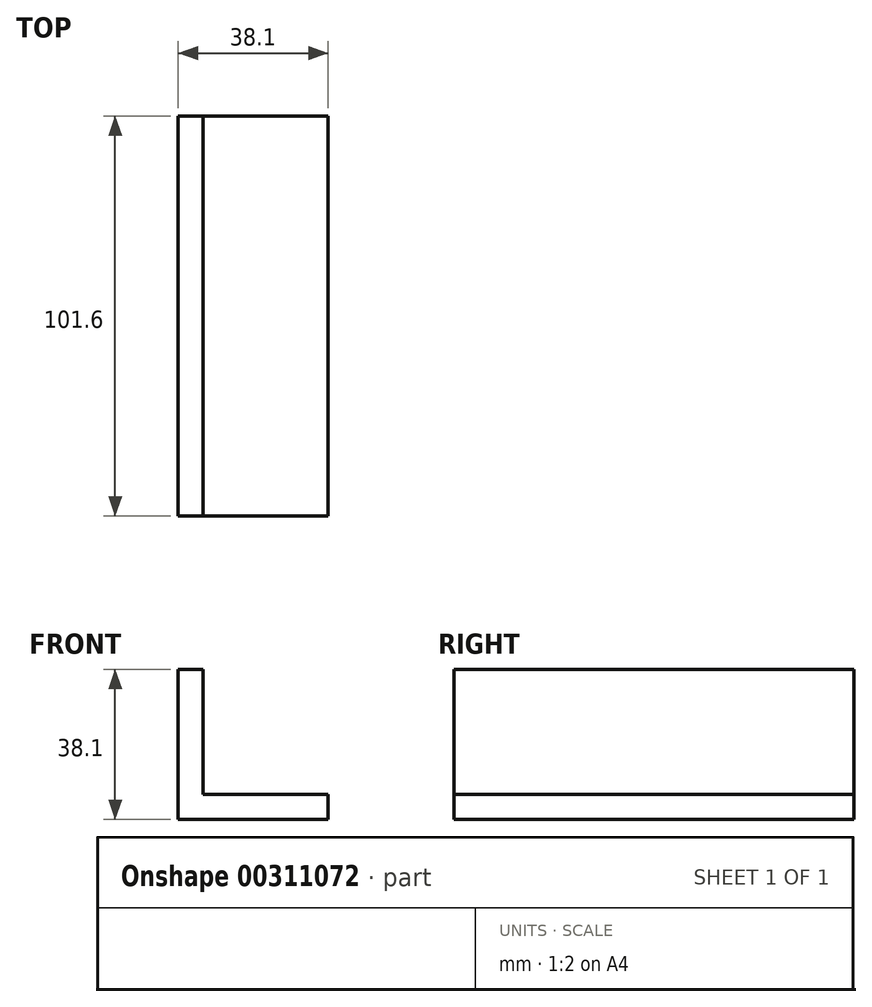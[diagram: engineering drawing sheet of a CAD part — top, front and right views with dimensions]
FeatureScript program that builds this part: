
annotation { "Feature Type Name" : "Feature", "Feature Type Description" : "" }
export const myFeature = defineFeature(function(context is Context, id is Id, definition is map)
    precondition{}
    {
        {
            var Q0;
            Q0=qCreatedBy(makeId("Front.planeOp"),FACE);
            var sketch = newSketch(context, id + "F0", { "sketchPlane" : qUnion([Q0])});
            skLineSegment(sketch, "E0", {"start": v(0, 0) * mm, "end": v(0, 38.1) * mm});
            skLineSegment(sketch, "E1", {"start": v(0, 38.1) * mm, "end": v(6.35, 38.1) * mm});
            skLineSegment(sketch, "E2", {"start": v(6.35, 38.1) * mm, "end": v(6.35, 6.35) * mm});
            skLineSegment(sketch, "E3", {"start": v(6.35, 6.35) * mm, "end": v(38.1, 6.35) * mm});
            skLineSegment(sketch, "E4", {"start": v(38.1, 6.35) * mm, "end": v(38.1, 0) * mm});
            skLineSegment(sketch, "E5", {"start": v(38.1, 0) * mm, "end": v(0, 0) * mm});
            skSolve(sketch);
        }
        {
            var Q0;
            Q0=qSketchRegion(id+"F0",true);
            extrude(context, id + "F1", {"entities" : qUnion([Q0]), "depth" : 101.6 * mm});
        }
    });
